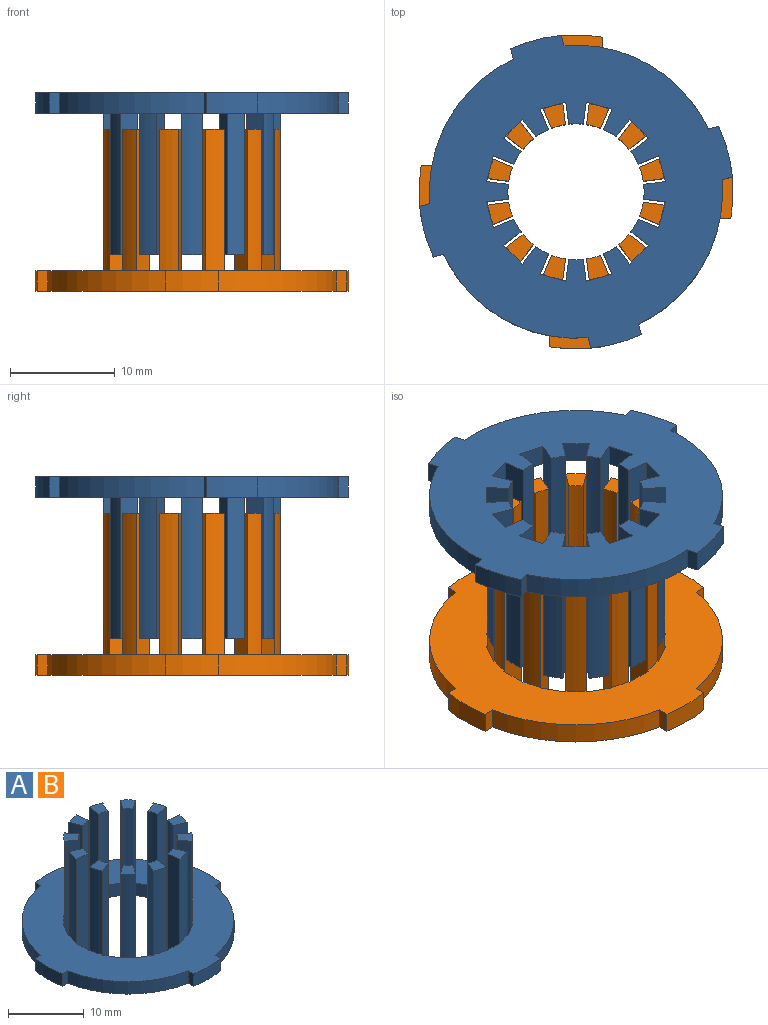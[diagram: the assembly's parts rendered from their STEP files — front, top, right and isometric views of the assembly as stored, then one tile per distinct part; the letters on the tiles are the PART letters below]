
ASSEMBLY  parts=2 mates=1
PART A: 90 faces, bbox 30x30x15.5 mm
  f0: plane 30x30mm, normal (0,0,1), area 407.6mm2, adj f2,f3,f4,f5,f8,f11,f14,f17
  f1: plane 30x30mm, normal (0,0,-1), area 447.4mm2, adj f2,f3,f4,f7,f10,f13,f16,f19
  f2: cylinder r=15mm len=5mm, axis (0,0,-1), area 10mm2, adj f0,f1,f84,f88
  f3: cylinder r=15mm len=5mm, axis (0,0,-1), area 10mm2, adj f0,f1,f81,f85
  f4: cylinder r=15mm len=5mm, axis (0,0,-1), area 10mm2, adj f0,f1,f80,f82
  f5: cylinder r=8.5mm len=13.5mm, axis (0,0,-1), area 26mm2, adj f0,f6,f74,f76
  f6: plane 2.57x2.57mm, normal (0,0,1), area 3.3mm2, adj f5,f7,f74,f76
  f7: cylinder r=6.5mm len=15.5mm, axis (0,0,1), area 21.5mm2, adj f1,f6,f74,f76
  f8: cylinder r=8.5mm len=13.5mm, axis (0,0,-1), area 26mm2, adj f0,f9,f71,f73
  f9: plane 2.34x2.11mm, normal (0,0,1), area 3.3mm2, adj f8,f10,f71,f73
  f10: cylinder r=6.5mm len=15.5mm, axis (0,0,1), area 21.5mm2, adj f1,f9,f71,f73
  f11: cylinder r=8.5mm len=13.5mm, axis (0,0,-1), area 26mm2, adj f0,f12,f68,f70
  f12: plane 2.34x2.11mm, normal (0,0,1), area 3.3mm2, adj f11,f13,f68,f70
  f13: cylinder r=6.5mm len=15.5mm, axis (0,0,1), area 21.5mm2, adj f1,f12,f68,f70
  f14: cylinder r=8.5mm len=13.5mm, axis (0,0,-1), area 26mm2, adj f0,f15,f65,f67
  f15: plane 2.57x2.57mm, normal (0,0,1), area 3.3mm2, adj f14,f16,f65,f67
  f16: cylinder r=6.5mm len=15.5mm, axis (0,0,1), area 21.5mm2, adj f1,f15,f65,f67
  f17: cylinder r=8.5mm len=13.5mm, axis (0,0,-1), area 26mm2, adj f0,f18,f62,f64
  f18: plane 2.34x2.11mm, normal (0,0,1), area 3.3mm2, adj f17,f19,f62,f64
  f19: cylinder r=6.5mm len=15.5mm, axis (0,0,1), area 21.5mm2, adj f1,f18,f62,f64
  f20: cylinder r=8.5mm len=13.5mm, axis (0,0,-1), area 26mm2, adj f0,f21,f59,f61
  f21: plane 2.34x2.11mm, normal (0,0,1), area 3.3mm2, adj f20,f22,f59,f61
  f22: cylinder r=6.5mm len=15.5mm, axis (0,0,1), area 21.5mm2, adj f1,f21,f59,f61
  f23: cylinder r=8.5mm len=13.5mm, axis (0,0,-1), area 26mm2, adj f0,f24,f56,f58
  f24: plane 2.57x2.57mm, normal (0,0,1), area 3.3mm2, adj f23,f25,f56,f58
  f25: cylinder r=6.5mm len=15.5mm, axis (0,0,1), area 21.5mm2, adj f1,f24,f56,f58
  f26: cylinder r=8.5mm len=13.5mm, axis (0,0,-1), area 26mm2, adj f0,f27,f53,f55
  f27: plane 2.34x2.11mm, normal (0,0,1), area 3.3mm2, adj f26,f28,f53,f55
  f28: cylinder r=6.5mm len=15.5mm, axis (0,0,1), area 21.5mm2, adj f1,f27,f53,f55
  f29: cylinder r=8.5mm len=13.5mm, axis (0,0,-1), area 26mm2, adj f0,f30,f50,f52
  f30: plane 2.34x2.11mm, normal (0,0,1), area 3.3mm2, adj f29,f31,f50,f52
  f31: cylinder r=6.5mm len=15.5mm, axis (0,0,1), area 21.5mm2, adj f1,f30,f50,f52
  f32: cylinder r=8.5mm len=13.5mm, axis (0,0,-1), area 26mm2, adj f0,f33,f47,f49
  f33: plane 2.57x2.57mm, normal (0,0,1), area 3.3mm2, adj f32,f34,f47,f49
  f34: cylinder r=6.5mm len=15.5mm, axis (0,0,1), area 21.5mm2, adj f1,f33,f47,f49
  f35: cylinder r=8.5mm len=13.5mm, axis (0,0,-1), area 26mm2, adj f0,f36,f44,f46
  f36: plane 2.34x2.11mm, normal (0,0,1), area 3.3mm2, adj f35,f37,f44,f46
  f37: cylinder r=6.5mm len=15.5mm, axis (0,0,1), area 21.5mm2, adj f1,f36,f44,f46
  f38: cylinder r=8.5mm len=13.5mm, axis (0,0,-1), area 26mm2, adj f0,f39,f43,f77
  f39: plane 2.34x2.11mm, normal (0,0,1), area 3.3mm2, adj f38,f41,f43,f77
  f40: cylinder r=15mm len=5mm, axis (0,0,-1), area 10mm2, adj f0,f1,f78,f87
  f41: cylinder r=6.5mm len=15.5mm, axis (0,0,1), area 21.5mm2, adj f1,f39,f43,f77
  f42: plane 2.54x2mm, normal (0,-1,0), area 5.1mm2, adj f0,f1,f43,f44
  f43: plane 15.5x2.09mm, normal (-0.99,0.13,0), area 31.2mm2, adj f0,f1,f38,f39,f41,f42
  f44: plane 15.5x2.09mm, normal (0.99,0.13,0), area 31.2mm2, adj f0,f1,f35,f36,f37,f42
  f45: plane 2.2x2mm, normal (0.5,-0.87,0), area 5.1mm2, adj f0,f1,f46,f47
  f46: plane 15.5x1.94mm, normal (-0.92,-0.39,0), area 31.2mm2, adj f0,f1,f35,f36,f37,f45
  f47: plane 15.5x1.67mm, normal (0.8,0.61,0), area 31.2mm2, adj f0,f1,f32,f33,f34,f45
  f48: plane 2.2x2mm, normal (0.87,-0.5,0), area 5.1mm2, adj f0,f1,f49,f50
  f49: plane 15.5x1.67mm, normal (-0.61,-0.8,0), area 31.2mm2, adj f0,f1,f32,f33,f34,f48
  f50: plane 15.5x1.94mm, normal (0.39,0.92,0), area 31.2mm2, adj f0,f1,f29,f30,f31,f48
  f51: plane 2.54x2mm, normal (1,0,0), area 5.1mm2, adj f0,f1,f52,f53
  f52: plane 15.5x2.09mm, normal (-0.13,-0.99,0), area 31.2mm2, adj f0,f1,f29,f30,f31,f51
  f53: plane 15.5x2.09mm, normal (-0.13,0.99,0), area 31.2mm2, adj f0,f1,f26,f27,f28,f51
  f54: plane 2.2x2mm, normal (0.87,0.5,0), area 5.1mm2, adj f0,f1,f55,f56
  f55: plane 15.5x1.94mm, normal (0.39,-0.92,0), area 31.2mm2, adj f0,f1,f26,f27,f28,f54
  f56: plane 15.5x1.67mm, normal (-0.61,0.8,0), area 31.2mm2, adj f0,f1,f23,f24,f25,f54
  f57: plane 2.2x2mm, normal (0.5,0.87,0), area 5.1mm2, adj f0,f1,f58,f59
  f58: plane 15.5x1.67mm, normal (0.8,-0.61,0), area 31.2mm2, adj f0,f1,f23,f24,f25,f57
  f59: plane 15.5x1.94mm, normal (-0.92,0.39,0), area 31.2mm2, adj f0,f1,f20,f21,f22,f57
  f60: plane 2.54x2mm, normal (0,1,0), area 5.1mm2, adj f0,f1,f61,f62
  f61: plane 15.5x2.09mm, normal (0.99,-0.13,0), area 31.2mm2, adj f0,f1,f20,f21,f22,f60
  f62: plane 15.5x2.09mm, normal (-0.99,-0.13,0), area 31.2mm2, adj f0,f1,f17,f18,f19,f60
  f63: plane 2.2x2mm, normal (-0.5,0.87,0), area 5.1mm2, adj f0,f1,f64,f65
  f64: plane 15.5x1.94mm, normal (0.92,0.39,0), area 31.2mm2, adj f0,f1,f17,f18,f19,f63
  f65: plane 15.5x1.67mm, normal (-0.8,-0.61,0), area 31.2mm2, adj f0,f1,f14,f15,f16,f63
  f66: plane 2.2x2mm, normal (-0.87,0.5,0), area 5.1mm2, adj f0,f1,f67,f68
  f67: plane 15.5x1.67mm, normal (0.61,0.8,0), area 31.2mm2, adj f0,f1,f14,f15,f16,f66
  f68: plane 15.5x1.94mm, normal (-0.39,-0.92,0), area 31.2mm2, adj f0,f1,f11,f12,f13,f66
  f69: plane 2.54x2mm, normal (-1,0,0), area 5.1mm2, adj f0,f1,f70,f71
  f70: plane 15.5x2.09mm, normal (0.13,0.99,0), area 31.2mm2, adj f0,f1,f11,f12,f13,f69
  f71: plane 15.5x2.09mm, normal (0.13,-0.99,0), area 31.2mm2, adj f0,f1,f8,f9,f10,f69
  f72: plane 2.2x2mm, normal (-0.87,-0.5,0), area 5.1mm2, adj f0,f1,f73,f74
  f73: plane 15.5x1.94mm, normal (-0.39,0.92,0), area 31.2mm2, adj f0,f1,f8,f9,f10,f72
  f74: plane 15.5x1.67mm, normal (0.61,-0.8,0), area 31.2mm2, adj f0,f1,f5,f6,f7,f72
  f75: plane 2.2x2mm, normal (-0.5,-0.87,0), area 5.1mm2, adj f0,f1,f76,f77
  f76: plane 15.5x1.67mm, normal (-0.8,0.61,0), area 31.2mm2, adj f0,f1,f5,f6,f7,f75
  f77: plane 15.5x1.94mm, normal (0.92,-0.39,0), area 31.2mm2, adj f0,f1,f38,f39,f41,f75
  f78: plane 2x1.02mm, normal (1,0,0), area 2mm2, adj f0,f1,f40,f79
  f79: cylinder r=14mm len=11.28mm, axis (0,0,1), area 33.9mm2, adj f0,f1,f78,f80
  f80: plane 2x1.02mm, normal (0,1,0), area 2mm2, adj f0,f1,f4,f79
  f81: plane 2x1.02mm, normal (1,0,0), area 2mm2, adj f0,f1,f3,f83
  f82: plane 2x1.02mm, normal (0,-1,0), area 2mm2, adj f0,f1,f4,f83
  f83: cylinder r=14mm len=11.28mm, axis (0,0,1), area 33.9mm2, adj f0,f1,f81,f82
  f84: plane 2x1.02mm, normal (0,-1,0), area 2mm2, adj f0,f1,f2,f86
  f85: plane 2x1.02mm, normal (-1,0,0), area 2mm2, adj f0,f1,f3,f86
  f86: cylinder r=14mm len=11.28mm, axis (0,0,1), area 33.9mm2, adj f0,f1,f84,f85
  f87: plane 2x1.02mm, normal (-1,0,0), area 2mm2, adj f0,f1,f40,f89
  f88: plane 2x1.02mm, normal (0,1,0), area 2mm2, adj f0,f1,f2,f89
  f89: cylinder r=14mm len=11.28mm, axis (0,0,1), area 33.9mm2, adj f0,f1,f87,f88
PART B: same geometry as A
PLACE A rot(axis=(0.99,0.13,0),180deg) t=(-17.42,-3.81,20.49)mm
PLACE B t=(-17.42,-3.81,1.49)mm
MATE revolute A.f7 <-> B.f7  axis (0,0,-1) through (-17.42,-3.81,18.49)mm
